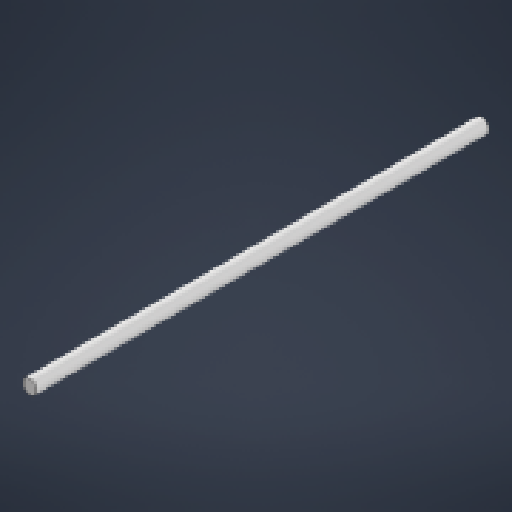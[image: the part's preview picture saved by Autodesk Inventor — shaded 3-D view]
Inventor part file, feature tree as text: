
AUTODESK INVENTOR PART (.ipt)
format: ipt  version: 2024.1 (Build 281209000, 209)  size: 130,048 bytes
history: native  units: in
note: dims shown in document units (in); Inventor stores cm internally (conversion verified against a paired STEP export)
features: extrude x1, sketch x1
ambient origin geometry x8: Origin, YZ Plane, XZ Plane, XY Plane, X Axis, Y Axis, Z Axis, Center Point
bodies: Solid1 (feature_tree)
feature tree (2):
  extrude  "Extrusion1"  Depth=7.874in TaperAngle=0.0deg
  sketch  "Sketch1"  dims[d0=0.25in d1=7.874in d2=0.0in]
